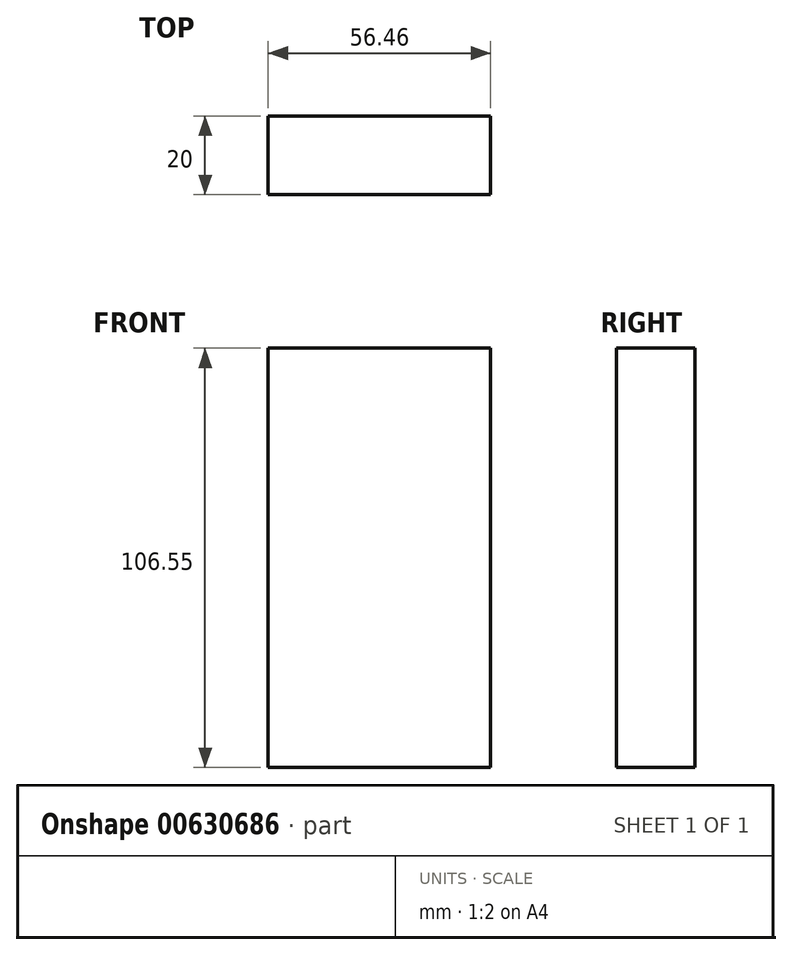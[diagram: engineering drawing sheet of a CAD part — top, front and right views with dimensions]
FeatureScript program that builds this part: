
annotation { "Feature Type Name" : "Feature", "Feature Type Description" : "" }
export const myFeature = defineFeature(function(context is Context, id is Id, definition is map)
    precondition{}
    {
        {
            var Q0;
            Q0=qCreatedBy(makeId("Front.planeOp"),FACE);
            var sketch = newSketch(context, id + "F0", { "sketchPlane" : qUnion([Q0])});
            skLineSegment(sketch, "E0.bottom", {"start": v(67.68, 62.2) * mm, "end": v(11.22, 62.2) * mm});
            skLineSegment(sketch, "E0.top", {"start": v(67.68, 168.76) * mm, "end": v(11.22, 168.76) * mm});
            skLineSegment(sketch, "E0.left", {"start": v(67.68, 62.2) * mm, "end": v(67.68, 168.76) * mm});
            skLineSegment(sketch, "E0.right", {"start": v(11.22, 62.2) * mm, "end": v(11.22, 168.76) * mm});
            skSolve(sketch);
        }
        {
            var Q0;
            Q0 = qSketchRegion(id + "F0", true);
            extrude(context, id + "F1", {"entities" : qUnion([Q0]), "depth" : 20 * mm, "offsetDistance" : 25 * mm});
        }
    });
